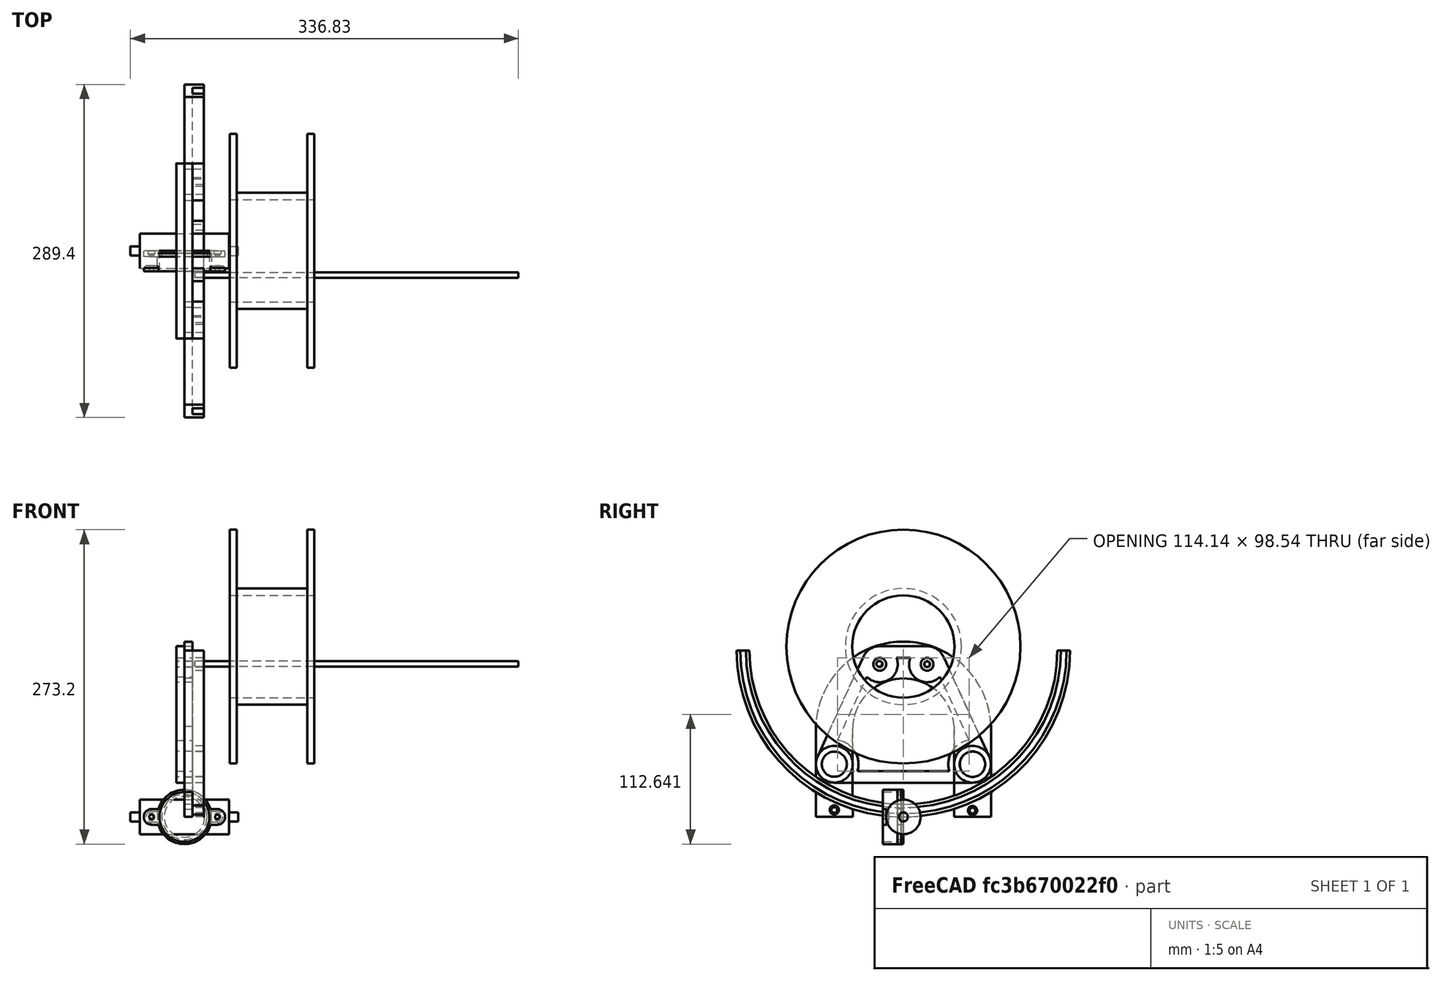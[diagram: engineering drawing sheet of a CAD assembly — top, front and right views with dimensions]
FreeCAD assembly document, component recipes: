
FREECAD ASSEMBLY — COMPONENT RECIPES ("filament dryer new version")

This assembly document has 17 components, labeled P0..P16 below (a component is one placed body or linked part). 17 of them carry a construction recipe — the FreeCAD feature program that regenerates the part from scratch, quoted from this document or its linked companion documents; the rest are supplied as boundary geometry only. No exploded tour is included for this assembly.
COMPONENT P0 — recipe-attached ("side bearing cilinders001", modeled in this document).
Construction recipe (the document's own serialized feature program — sketch geometry with constraints, then the solid features built on it; lengths are millimeters unless a unit is written):

FEATURE [Sketcher::SketchObject] Sketch004
  ArcFitTolerance = 1e-06
  AttachmentSupport = -> [XZ_Plane003]
  FullyConstrained = true
  MakeInternals = false
  MapMode = 5
  Placement = pos=(0,0,0) rot=(1,0,0;1.5708rad)
  expr: Constraints[17] = 3.925 mm
  sketch-geometry (8):
    g0: LineSegment StartX=-46.8333 StartY=0 StartZ=0 EndX=-46.8333 EndY=3.925 EndZ=0
    g1: LineSegment StartX=-46.8333 StartY=3.925 StartZ=0 EndX=-38.8333 EndY=3.925 EndZ=0
    g2: LineSegment StartX=-38.8333 StartY=3.925 StartZ=0 EndX=-38.8333 EndY=15 EndZ=0
    g3: LineSegment StartX=-38.8333 StartY=15 StartZ=0 EndX=38.8333 EndY=15 EndZ=0
    g4: LineSegment StartX=38.8333 StartY=15 StartZ=0 EndX=38.8333 EndY=3.925 EndZ=0
    g5: LineSegment StartX=38.8333 StartY=3.925 StartZ=0 EndX=46.8333 EndY=3.925 EndZ=0
    g6: LineSegment StartX=46.8333 StartY=3.925 StartZ=0 EndX=46.8333 EndY=1.2372e-12 EndZ=0
    g7: LineSegment StartX=-46.8333 StartY=0 StartZ=0 EndX=46.8333 EndY=1.2372e-12 EndZ=0
  constraints (23):
    c: PointOnObject(g0,g-1)
    c: Vertical(g0)
    c: Coincident(g1,g0)
    c: Horizontal(g1)
    c: Coincident(g2,g1)
    c: Vertical(g2)
    c: Coincident(g3,g2)
    c: Coincident(g4,g3)
    c: Coincident(g5,g4)
    c: Horizontal(g5)
    c: Vertical(g6)
    c: Vertical(g4)
    c: Equal(g2,g4)
    c: Equal(g0,g6)
    c: Symmetric(g2,g3,g-2)
    c: Coincident(g6,g5)
    c: DistanceX(g1,g1) = 8
    c: DistanceY(g0,g0) = 3.925
    c: Distance(g2,g-1) = 15
    c: Coincident(g7,g0)
    c: Coincident(g7,g6)
    c: DistanceX(g7,g7) = 93.6666
    c: Equal(g1,g5)
FEATURE [PartDesign::Revolution] Revolution001
  Angle = 360
  Angle2 = 60
  Axis = (1,0,0)
  Base = (0,0,0)
  Placement = pos=(0,0,0) rot=(1,0,0;1.5708rad)
  Profile = -> Sketch004
  ReferenceAxis = -> X_Axis003
  Refine = true
  Suppressed = false
  Type = 0
FEATURE [PartDesign::Body] Body003  label="side bearing cilinders"
  AllowCompound = false
  Group = -> [Sketch004,Revolution001]
  Origin = -> Origin003
  Tip = -> Revolution001
COMPONENT P1 — same part as P0; its construction recipe is shown at P0.
COMPONENT P2 — same part as P0; its construction recipe is shown at P0.
COMPONENT P3 — same part as P0; its construction recipe is shown at P0.
COMPONENT P4 — same part as P0; its construction recipe is shown at P0.
COMPONENT P5 — same part as P0; its construction recipe is shown at P0.
COMPONENT P6 — recipe-attached ("spool filament001", modeled in this document).
Construction recipe (the document's own serialized feature program — sketch geometry with constraints, then the solid features built on it; lengths are millimeters unless a unit is written):

FEATURE [Sketcher::SketchObject] Sketch
  ArcFitTolerance = 1e-06
  AttachmentSupport = -> [XZ_Plane]
  FullyConstrained = false
  MakeInternals = false
  MapMode = 5
  Placement = pos=(0,0,0) rot=(1,0,0;1.5708rad)
  sketch-geometry (8):
    g0: LineSegment StartX=-36.586 StartY=44.45 StartZ=0 EndX=36.586 EndY=44.45 EndZ=0
    g1: LineSegment StartX=-36.586 StartY=44.45 StartZ=0 EndX=-36.586 EndY=101.6 EndZ=0
    g2: LineSegment StartX=36.586 StartY=44.45 StartZ=0 EndX=36.586 EndY=101.6 EndZ=0
    g3: LineSegment StartX=-36.586 StartY=101.6 StartZ=0 EndX=-30.586 EndY=101.6 EndZ=0
    g4: LineSegment StartX=-30.586 StartY=101.6 StartZ=0 EndX=-30.586 EndY=50.45 EndZ=0
    g5: LineSegment StartX=30.586 StartY=101.6 StartZ=0 EndX=30.586 EndY=50.45 EndZ=0
    g6: LineSegment StartX=30.586 StartY=101.6 StartZ=0 EndX=36.586 EndY=101.6 EndZ=0
    g7: LineSegment StartX=-30.586 StartY=50.45 StartZ=0 EndX=30.586 EndY=50.45 EndZ=0
  constraints (21):
    c: Distance(g0) = 73.172
    c: Distance(g-1,g0) = 44.45
    c: Symmetric(g0,g0,g-2)
    c: Coincident(g1,g0)
    c: Vertical(g1)
    c: Coincident(g2,g0)
    c: Vertical(g2)
    c: Distance(g1,g-1) = 101.6
    c: Coincident(g3,g1)
    c: Coincident(g6,g2)
    c: Horizontal(g3)
    c: Vertical(g4)
    c: Vertical(g5)
    c: Symmetric(g5,g4,g-2)
    c: Distance(g1,g4) = 6
    c: Coincident(g3,g4)
    c: PointOnObject(g6,g5)
    c: Horizontal(g7)
    c: Distance(g0,g7) = 6
    c: Coincident(g4,g7)
    c: Coincident(g5,g7)
FEATURE [PartDesign::Revolution] Revolution
  Angle = 360
  Angle2 = 60
  Axis = (1,0,0)
  Base = (0,0,0)
  Placement = pos=(0,0,0) rot=(1,0,0;1.5708rad)
  Profile = -> Sketch
  ReferenceAxis = -> X_Axis
  Refine = true
  Reversed = true
  Suppressed = false
  Type = 0
FEATURE [PartDesign::Body] Body  label="spool filament"
  AllowCompound = false
  Group = -> [Sketch,Revolution]
  Origin = -> Origin
  Placement = pos=(76,0,148) rot=(0,0,1;0rad)
  Tip = -> Revolution
COMPONENT P7 — same part as P6; its construction recipe is shown at P6.
COMPONENT P8 — same part as P6; its construction recipe is shown at P6.
COMPONENT P9 — recipe-attached ("spool holder001", modeled in this document).
Construction recipe (the document's own serialized feature program — sketch geometry with constraints, then the solid features built on it; lengths are millimeters unless a unit is written):

FEATURE [Sketcher::SketchObject] Sketch001
  ArcFitTolerance = 1e-06
  AttachmentSupport = -> [YZ_Plane001]
  FullyConstrained = false
  MakeInternals = false
  MapMode = 5
  Placement = pos=(0,0,0) rot=(0.57735,0.57735,0.57735;2.0944rad)
  expr: Constraints[3] = 133.7 * 2 mm
  sketch-geometry (31):
    g0: Circle CenterX=-60 CenterY=45.7733 CenterZ=0 NormalX=0 NormalY=0 NormalZ=1 AngleXU=0 Radius=11.075
    g1: Circle CenterX=60 CenterY=45.7733 CenterZ=0 NormalX=0 NormalY=0 NormalZ=1 AngleXU=0 Radius=11.075
    g2: ArcOfCircle CenterX=0 CenterY=144.7 CenterZ=0 NormalX=0 NormalY=0 NormalZ=1 AngleXU=0 Radius=133.7 StartAngle=3.14159 EndAngle=4.10707
    g3: LineSegment [constr] StartX=-133.7 StartY=144.7 StartZ=0 EndX=133.7 EndY=144.7 EndZ=0
    g4: LineSegment [constr] StartX=-133.7 StartY=144.7 StartZ=0 EndX=133.7 EndY=144.7 EndZ=0
    g5: ArcOfCircle CenterX=0 CenterY=144.7 CenterZ=0 NormalX=0 NormalY=0 NormalZ=1 AngleXU=0 Radius=144.7 StartAngle=3.14159 EndAngle=4.15941
    g6: LineSegment StartX=-133.7 StartY=144.7 StartZ=0 EndX=-144.7 EndY=144.7 EndZ=0
    g7: LineSegment StartX=133.7 StartY=144.7 StartZ=0 EndX=144.7 EndY=144.7 EndZ=0
    g8: LineSegment StartX=-76.0782 StartY=46.2231 StartZ=0 EndX=-76.0782 EndY=34.7555 EndZ=0
    g9: LineSegment StartX=76.0296 StartY=48.9403 StartZ=0 EndX=76.0296 EndY=34.7219 EndZ=0
    g10: LineSegment StartX=-76 StartY=21.5656 StartZ=0 EndX=-76 EndY=0 EndZ=0
    g11: LineSegment StartX=76 StartY=21.5656 StartZ=0 EndX=76 EndY=0 EndZ=0
    g12: LineSegment StartX=-44.0838 StartY=46.2231 StartZ=0 EndX=-44.0838 EndY=18.4768 EndZ=0
    g13: LineSegment StartX=44 StartY=48.9403 StartZ=0 EndX=44 EndY=18.4475 EndZ=0
    g14: LineSegment StartX=-44 StartY=6.85193 StartZ=0 EndX=-44 EndY=0 EndZ=0
    g15: LineSegment StartX=43.9992 StartY=6.85167 StartZ=0 EndX=43.9992 EndY=0 EndZ=0
    g16: LineSegment StartX=-76 StartY=0 StartZ=0 EndX=-44 EndY=0 EndZ=0
    g17: LineSegment StartX=43.9992 StartY=0 StartZ=0 EndX=76 EndY=0 EndZ=0
    g18: ArcOfCircle CenterX=0 CenterY=144.7 CenterZ=0 NormalX=0 NormalY=0 NormalZ=1 AngleXU=0 Radius=144.7 StartAngle=4.40342 EndAngle=5.02135
    g19: ArcOfCircle CenterX=0 CenterY=144.7 CenterZ=0 NormalX=0 NormalY=0 NormalZ=1 AngleXU=0 Radius=144.7 StartAngle=5.26537 EndAngle=6.28319
    g20: ArcOfCircle CenterX=0 CenterY=144.7 CenterZ=0 NormalX=0 NormalY=0 NormalZ=1 AngleXU=0 Radius=133.7 StartAngle=5.31726 EndAngle=6.28319
    g21: ArcOfCircle CenterX=0 CenterY=144.7 CenterZ=0 NormalX=0 NormalY=0 NormalZ=1 AngleXU=0 Radius=133.7 StartAngle=4.37638 EndAngle=5.04773
    g22: LineSegment [constr] StartX=-76.0782 StartY=46.2231 StartZ=0 EndX=-44.0838 EndY=46.2231 EndZ=0
    g23: LineSegment [constr] StartX=44 StartY=48.9403 StartZ=0 EndX=76.0296 EndY=48.9403 EndZ=0
    g24: LineSegment StartX=-76.0782 StartY=46.2231 StartZ=0 EndX=-76.0782 EndY=76.2231 EndZ=0
    g25: LineSegment StartX=76.0296 StartY=48.9403 StartZ=0 EndX=76.0296 EndY=78.9403 EndZ=0
    g26: LineSegment StartX=44 StartY=48.9403 StartZ=0 EndX=44 EndY=78.9403 EndZ=0
    g27: LineSegment StartX=-44.0838 StartY=46.2231 StartZ=0 EndX=-44.0838 EndY=76.2231 EndZ=0
    g28: LineSegment [constr] StartX=-44.0838 StartY=76.2231 StartZ=0 EndX=0 EndY=76.2231 EndZ=0
    g29: ArcOfCircle CenterX=0 CenterY=76.2231 CenterZ=0 NormalX=0 NormalY=0 NormalZ=1 AngleXU=0 Radius=44.0838 StartAngle=0.061677 EndAngle=3.14159
    g30: ArcOfCircle CenterX=0 CenterY=76.2231 CenterZ=0 NormalX=0 NormalY=0 NormalZ=1 AngleXU=0 Radius=76.0782 StartAngle=0.0357239 EndAngle=3.14159
  constraints (80):
    c: Diameter(g0) = 22.15
    c: Equal(g1,g0)
    c: Symmetric(g0,g1,g-2)
    c: Diameter(g2) = 267.4
    c: PointOnObject(g2,g-2)
    c: Horizontal(g3)
    c: PointOnObject(g2,g3)
    c: Coincident(g4,g3)
    c: Coincident(g4,g3)
    c: Coincident(g20,g3)
    c: Coincident(g2,g3)
    c: Distance(g2,g-1) = 11
    c: Coincident(g5,g2)
    c: PointOnObject(g-1,g18)
    c: Coincident(g6,g2)
    c: Horizontal(g6)
    c: Coincident(g7,g20)
    c: Horizontal(g7)
    c: Coincident(g19,g7)
    c: Coincident(g5,g6)
    c: PointOnObject(g10,g-1)
    c: Vertical(g8)
    c: PointOnObject(g11,g-1)
    c: Vertical(g9)
    c: Distance(g0,g-2) = 60
    c: PointOnObject(g9,g20)
    c: PointOnObject(g11,g19)
    c: PointOnObject(g14,g-1)
    c: Vertical(g12)
    c: PointOnObject(g15,g-1)
    c: Vertical(g13)
    c: PointOnObject(g12,g21)
    c: PointOnObject(g14,g18)
    c: Coincident(g16,g10)
    c: Coincident(g16,g14)
    c: Coincident(g17,g15)
    c: Coincident(g17,g11)
    c: Equal(g5,g18)
    c: Coincident(g5,g10)
    c: PointOnObject(g18,g14)
    c: Coincident(g5,g18)
    c: Equal(g18,g19)
    c: Coincident(g18,g15)
    c: PointOnObject(g19,g11)
    c: Coincident(g18,g19)
    c: Equal(g2,g20)
    c: Coincident(g21,g13)
    c: PointOnObject(g20,g9)
    c: Coincident(g2,g20)
    c: Equal(g2,g21)
    c: Coincident(g2,g8)
    c: PointOnObject(g21,g12)
    c: Coincident(g2,g21)
    c: Coincident(g22,g8)
    c: Coincident(g22,g12)
    c: Horizontal(g22)
    c: Coincident(g23,g13)
    c: Coincident(g23,g9)
    c: Horizontal(g23)
    c: Distance(g24) = 30
    c: Coincident(g24,g8)
    c: Vertical(g24)
    c: Coincident(g25,g9)
    c: Vertical(g25)
    c: Coincident(g26,g13)
    c: Vertical(g26)
    c: Coincident(g27,g12)
    c: Vertical(g27)
    c: Equal(g24,g27)
    c: Equal(g27,g26)
    c: Equal(g26,g25)
    c: Coincident(g28,g27)
    c: PointOnObject(g28,g-2)
    c: Horizontal(g28)
    c: Coincident(g29,g28)
    c: Coincident(g29,g27)
    c: Coincident(g29,g26)
    c: Coincident(g30,g28)
    c: Coincident(g30,g24)
    c: Coincident(g30,g25)
FEATURE [PartDesign::Pad] Pad
  Direction = (1,0,0)
  Length = 7
  Length2 = 10
  Placement = pos=(0,0,0) rot=(1,1,1;2.0944rad)
  Profile = -> Sketch001
  ReferenceAxis = -> Sketch001 [N_Axis]
  Refine = true
  Suppressed = false
  Type = 0
FEATURE [Sketcher::SketchObject] Sketch002
  ArcFitTolerance = 1e-06
  AttachmentSupport = -> [Pad]
  ExternalGeometry = -> [Pad]
  FullyConstrained = false
  MakeInternals = false
  MapMode = 5
  Placement = pos=(7,0,0) rot=(0.57735,0.57735,0.57735;2.0944rad)
  sketch-geometry (24):
    g0: ArcOfCircle CenterX=2.39e-14 CenterY=144.7 CenterZ=0 NormalX=0 NormalY=0 NormalZ=1 AngleXU=0 Radius=133.7 StartAngle=3.14159 EndAngle=6.28319
    g1: ArcOfCircle CenterX=2.39e-14 CenterY=144.7 CenterZ=0 NormalX=0 NormalY=0 NormalZ=1 AngleXU=0 Radius=144.7 StartAngle=3.14159 EndAngle=6.28319
    g2: ArcOfCircle CenterX=2.39e-14 CenterY=144.7 CenterZ=0 NormalX=0 NormalY=0 NormalZ=1 AngleXU=0 Radius=141.7 StartAngle=3.14159 EndAngle=6.28319
    g3: ArcOfCircle CenterX=2.39e-14 CenterY=144.7 CenterZ=0 NormalX=0 NormalY=0 NormalZ=1 AngleXU=0 Radius=136.7 StartAngle=3.14159 EndAngle=6.28319
    g4: LineSegment StartX=133.7 StartY=144.7 StartZ=0 EndX=136.7 EndY=144.7 EndZ=0
    g5: LineSegment StartX=141.7 StartY=144.7 StartZ=0 EndX=144.7 EndY=144.7 EndZ=0
    g6: LineSegment StartX=-136.7 StartY=144.7 StartZ=0 EndX=-133.7 EndY=144.7 EndZ=0
    g7: LineSegment StartX=-144.7 StartY=144.7 StartZ=0 EndX=-141.7 EndY=144.7 EndZ=0
    g8: Circle CenterX=-60 CenterY=6 CenterZ=0 NormalX=0 NormalY=0 NormalZ=1 AngleXU=0 Radius=2.5
    g9: Circle CenterX=-60 CenterY=6 CenterZ=0 NormalX=0 NormalY=0 NormalZ=1 AngleXU=0 Radius=4
    g10: LineSegment [constr] StartX=-60 StartY=10.7501 StartZ=0 EndX=-60 EndY=-7.18174 EndZ=0
    g11: Circle CenterX=60 CenterY=5.5 CenterZ=0 NormalX=0 NormalY=0 NormalZ=1 AngleXU=0 Radius=2.5
    g12: Circle CenterX=60 CenterY=5.5 CenterZ=0 NormalX=0 NormalY=0 NormalZ=1 AngleXU=0 Radius=4
    g13: Circle CenterX=-60 CenterY=45.7733 CenterZ=0 NormalX=0 NormalY=0 NormalZ=1 AngleXU=0 Radius=10.901
    g14: Circle CenterX=-60 CenterY=45.7733 CenterZ=0 NormalX=0 NormalY=0 NormalZ=1 AngleXU=0 Radius=16
    g15: Circle CenterX=59.9992 CenterY=45.7733 CenterZ=0 NormalX=0 NormalY=0 NormalZ=1 AngleXU=0 Radius=16
    g16: Circle CenterX=59.9992 CenterY=45.7733 CenterZ=0 NormalX=0 NormalY=0 NormalZ=1 AngleXU=0 Radius=11.0656
    g17: LineSegment [constr] StartX=0 StartY=152.301 StartZ=0 EndX=0 EndY=120.307 EndZ=0
    g18: LineSegment [constr] StartX=0 StartY=136.304 StartZ=0 EndX=37.5871 EndY=136.304 EndZ=0
    g19: Circle CenterX=-20.575 CenterY=132.671 CenterZ=0 NormalX=0 NormalY=0 NormalZ=1 AngleXU=0 Radius=2.575
    g20: Circle CenterX=-20.575 CenterY=132.671 CenterZ=0 NormalX=0 NormalY=0 NormalZ=1 AngleXU=0 Radius=5.575
    g21: ArcOfCircle [constr] CenterX=8.5e-15 CenterY=76.2231 CenterZ=0 NormalX=0 NormalY=0 NormalZ=1 AngleXU=0 Radius=60.081 StartAngle=0.738747 EndAngle=2.47765
    g22: Circle CenterX=20.575 CenterY=132.671 CenterZ=0 NormalX=0 NormalY=0 NormalZ=1 AngleXU=0 Radius=5.575
    g23: Circle CenterX=20.575 CenterY=132.671 CenterZ=0 NormalX=0 NormalY=0 NormalZ=1 AngleXU=0 Radius=2.575
  constraints (50):
    c: Coincident(g0,g-5)
    c: Coincident(g0,g-3)
    c: Coincident(g0,g-4)
    c: Coincident(g1,g0)
    c: Coincident(g1,g-3)
    c: Coincident(g1,g-4)
    c: Coincident(g2,g0)
    c: PointOnObject(g2,g-3)
    c: PointOnObject(g2,g-4)
    c: Coincident(g3,g0)
    c: PointOnObject(g3,g-3)
    c: PointOnObject(g3,g-4)
    c: Distance(g2,g1) = 3
    c: Distance(g3,g0) = 3
    c: Coincident(g4,g0)
    c: Coincident(g4,g3)
    c: Coincident(g5,g2)
    c: Coincident(g5,g1)
    c: Coincident(g6,g3)
    c: Coincident(g6,g0)
    c: Coincident(g7,g1)
    c: Coincident(g7,g2)
    c: Coincident(g9,g8)
    c: Diameter(g8) = 5
    c: Distance(g9,g-1) = 2
    c: Symmetric(g-7,g-6,g10)
    c: PointOnObject(g8,g10)
    c: Coincident(g12,g11)
    c: Diameter(g11) = 5
    c: Diameter(g12) = 8
    c: Tangent(g13,g-8) = -1.5708
    c: Coincident(g14,g13)
    c: Coincident(g16,g15)
    c: PointOnObject(g17,g-2)
    c: PointOnObject(g17,g-2)
    c: PointOnObject(g17,g-10)
    c: PointOnObject(g17,g-11)
    c: Symmetric(g17,g17,g18)
    c: PointOnObject(g18,g17)
    c: Diameter(g19) = 5.15
    c: Coincident(g20,g19)
    c: Distance(g20,g19) = 3
    c: Coincident(g21,g-11)
    c: PointOnObject(g18,g21)
    c: PointOnObject(g19,g21)
    c: Distance(g20,g17) = 15
    c: Diameter(g23) = 5.15
    c: Coincident(g22,g23)
    c: Distance(g22,g23) = 3
    c: Equal(g9,g12)
FEATURE [PartDesign::Pad] Pad001
  BaseFeature = -> Pad
  Direction = (1,0,0)
  Length = 10
  Length2 = 10
  Placement = pos=(0,0,0) rot=(1,1,1;2.0944rad)
  Profile = -> Sketch002
  ReferenceAxis = -> Sketch002 [N_Axis]
  Refine = true
  Suppressed = false
  Type = 0
FEATURE [PartDesign::Body] Body001  label="spool holder"
  AllowCompound = false
  Group = -> [Sketch001,Pad,Sketch002,Pad001]
  Origin = -> Origin001
  Tip = -> Pad001
COMPONENT P10 — same part as P9; its construction recipe is shown at P9.
COMPONENT P11 — recipe-attached ("spoon holder joins001", modeled in this document).
Construction recipe (the document's own serialized feature program — sketch geometry with constraints, then the solid features built on it; lengths are millimeters unless a unit is written):

FEATURE [Sketcher::SketchObject] Sketch003
  ArcFitTolerance = 1e-06
  AttachmentSupport = -> [YZ_Plane002]
  FullyConstrained = false
  MakeInternals = false
  MapMode = 5
  Placement = pos=(0,0,0) rot=(0.57735,0.57735,0.57735;2.0944rad)
  sketch-geometry (2):
    g0: Circle [constr] CenterX=0 CenterY=0 CenterZ=0 NormalX=0 NormalY=0 NormalZ=1 AngleXU=0 Radius=0
    g1: Circle CenterX=0 CenterY=0 CenterZ=0 NormalX=0 NormalY=0 NormalZ=1 AngleXU=0 Radius=2.5
  constraints (2):
    c: Coincident(g1,g0)
    c: Diameter(g1) = 5
FEATURE [PartDesign::Pad] Pad002
  Direction = (1,0,0)
  Length = 281
  Length2 = 10
  Placement = pos=(0,0,0) rot=(1,1,1;2.0944rad)
  Profile = -> Sketch003
  ReferenceAxis = -> Sketch003 [N_Axis]
  Refine = true
  Suppressed = false
  Type = 0
FEATURE [PartDesign::Body] Body002  label="spoon holder joins"
  AllowCompound = false
  Group = -> [Sketch003,Pad002]
  Origin = -> Origin002
  Placement = pos=(9,-21,133) rot=(0,0,1;0rad)
  Tip = -> Pad002
COMPONENT P12 — same part as P11; its construction recipe is shown at P11.
COMPONENT P13 — same part as P11; its construction recipe is shown at P11.
COMPONENT P14 — same part as P11; its construction recipe is shown at P11.
COMPONENT P15 — recipe-attached ("spoon holder middle section001", modeled in this document).
Construction recipe (the document's own serialized feature program — sketch geometry with constraints, then the solid features built on it; lengths are millimeters unless a unit is written):

FEATURE [PartDesign::SubShapeBinder] Binder
  BindCopyOnChange = 0
  BindMode = 0
  ClaimChildren = false
  Context = -> Body004 [Binder.]
  Fuse = false
  MakeFace = true
  OffsetFill = false
  OffsetIntersection = false
  OffsetJoinType = 0
  OffsetOpenResult = false
  PartialLoad = false
  Refine = true
  Relative = true
  Support = -> [Body001[Pad001.Face33,Pad001.Face34]]
  _Version = 2
FEATURE [Sketcher::SketchObject] Sketch005
  ArcFitTolerance = 1e-06
  AttachmentSupport = -> [YZ_Plane004]
  ExternalGeometry = -> [Binder]
  FullyConstrained = false
  MakeInternals = false
  MapMode = 5
  Placement = pos=(0,0,0) rot=(0.57735,0.57735,0.57735;2.0944rad)
  sketch-geometry (24):
    g0: Circle CenterX=-60 CenterY=45.77 CenterZ=0 NormalX=0 NormalY=0 NormalZ=1 AngleXU=0 Radius=11
    g1: Circle CenterX=59.9999 CenterY=45.77 CenterZ=0 NormalX=0 NormalY=0 NormalZ=1 AngleXU=0 Radius=11
    g2: LineSegment [constr] StartX=-60 StartY=45.77 StartZ=0 EndX=-60 EndY=0 EndZ=0
    g3: ArcOfCircle CenterX=-60 CenterY=45.77 CenterZ=0 NormalX=0 NormalY=0 NormalZ=1 AngleXU=0 Radius=16 StartAngle=2.71191 EndAngle=4.71239
    g4: ArcOfCircle CenterX=59.9999 CenterY=45.77 CenterZ=0 NormalX=0 NormalY=0 NormalZ=1 AngleXU=0 Radius=16 StartAngle=4.71239 EndAngle=6.71287
    g5: LineSegment StartX=-39.8754 StartY=39.77 StartZ=0 EndX=39.8753 EndY=39.77 EndZ=0
    g6: ArcOfCircle CenterX=59.9999 CenterY=45.77 CenterZ=0 NormalX=0 NormalY=0 NormalZ=1 AngleXU=0 Radius=21 StartAngle=1.71073 EndAngle=3.43134
    g7: ArcOfCircle CenterX=-60 CenterY=45.77 CenterZ=0 NormalX=0 NormalY=0 NormalZ=1 AngleXU=0 Radius=21 StartAngle=5.99343 EndAngle=7.71405
    g8: GeomPoint [constr] X=0 Y=151.304 Z=0
    g9: Circle CenterX=-20.575 CenterY=132.671 CenterZ=0 NormalX=0 NormalY=0 NormalZ=1 AngleXU=0 Radius=2.575
    g10: Circle CenterX=20.575 CenterY=132.671 CenterZ=0 NormalX=0 NormalY=0 NormalZ=1 AngleXU=0 Radius=2.36628
    g11: Circle [constr] CenterX=-20.575 CenterY=132.671 CenterZ=0 NormalX=0 NormalY=0 NormalZ=1 AngleXU=0 Radius=5.63976
    g12: Circle [constr] CenterX=20.575 CenterY=132.671 CenterZ=0 NormalX=0 NormalY=0 NormalZ=1 AngleXU=0 Radius=5.575
    g13: LineSegment StartX=-74.5456 StartY=52.4353 StartZ=0 EndX=-34.7931 EndY=139.186 EndZ=0
    g14: LineSegment StartX=74.5455 StartY=52.4353 StartZ=0 EndX=34.7931 EndY=139.186 EndZ=0
    g15: ArcOfCircle CenterX=-20.575 CenterY=132.671 CenterZ=0 NormalX=0 NormalY=0 NormalZ=1 AngleXU=0 Radius=15.6398 StartAngle=3.91379 EndAngle=6.6521
    g16: ArcOfCircle CenterX=20.575 CenterY=132.671 CenterZ=0 NormalX=0 NormalY=0 NormalZ=1 AngleXU=0 Radius=15.6398 StartAngle=0.429681 EndAngle=1.5708
    g17: LineSegment StartX=-57.071 StartY=66.5647 StartZ=0 EndX=-31.779 EndY=121.759 EndZ=0
    g18: LineSegment StartX=57.071 StartY=66.5647 StartZ=0 EndX=31.779 EndY=121.759 EndZ=0
    g19: LineSegment StartX=-5.9875 StartY=138.311 StartZ=0 EndX=5.9875 EndY=138.311 EndZ=0
    g20: ArcOfCircle CenterX=-20.575 CenterY=132.671 CenterZ=0 NormalX=0 NormalY=0 NormalZ=1 AngleXU=0 Radius=15.6398 StartAngle=1.5708 EndAngle=2.71191
    g21: ArcOfCircle CenterX=20.575 CenterY=132.671 CenterZ=0 NormalX=0 NormalY=0 NormalZ=1 AngleXU=0 Radius=15.6398 StartAngle=2.77268 EndAngle=5.51099
    g22: LineSegment StartX=-20.575 StartY=148.311 StartZ=0 EndX=20.575 EndY=148.311 EndZ=0
    g23: LineSegment StartX=-60 StartY=29.77 StartZ=0 EndX=59.9999 EndY=29.77 EndZ=0
  constraints (52):
    c: Diameter(g0) = 22
    c: PointOnObject(g2,g-1)
    c: Block(g1)
    c: PointOnObject(g3,g2)
    c: Distance(g0,g3) = 5
    c: Distance(g1,g4) = 5
    c: Block(g2)
    c: Coincident(g0,g2)
    c: Coincident(g3,g0)
    c: Coincident(g4,g1)
    c: Horizontal(g5)
    c: Coincident(g6,g1)
    c: Coincident(g6,g5)
    c: Coincident(g7,g0)
    c: Coincident(g7,g5)
    c: Distance(g0,g7) = 10
    c: Distance(g6,g1) = 10
    c: PointOnObject(g8,g-2)
    c: Coincident(g9,g-5)
    c: Equal(g9,g-5)
    c: Coincident(g10,g-4)
    c: Coincident(g11,g9)
    c: Coincident(g12,g10)
    c: Tangent(g12,g-4)
    c: Coincident(g15,g9)
    c: Coincident(g16,g10)
    c: Distance(g11,g15) = 10
    c: Block(g11)
    c: Tangent(g4,g14) = -1.5708
    c: Tangent(g3,g13) = 1.5708
    c: Coincident(g17,g7)
    c: Coincident(g18,g6)
    c: Parallel(g18,g14)
    c: Parallel(g17,g13)
    c: Distance(g13,g17) = 10
    c: Distance(g14,g18) = 10
    c: Coincident(g20,g13) = 1.5708
    c: Coincident(g15,g17)
    c: Coincident(g21,g18)
    c: Tangent(g16,g14) = -1.5708
    c: PointOnObject(g19,g21)
    c: Coincident(g15,g19)
    c: Coincident(g15,g20)
    c: Equal(g16,g21)
    c: PointOnObject(g21,g19)
    c: Coincident(g16,g21)
    c: Coincident(g22,g20)
    c: Coincident(g22,g16)
    c: Horizontal(g22)
    c: Coincident(g23,g3)
    c: Tangent(g23,g4) = -1.5708
    c: Horizontal(g23)
FEATURE [PartDesign::Pad] Pad008
  Direction = (1,0,0)
  Length = 14
  Length2 = 10
  Midplane = true
  Placement = pos=(0,0,0) rot=(1,1,1;2.0944rad)
  Profile = -> Sketch005
  ReferenceAxis = -> Sketch005 [N_Axis]
  Refine = true
  Suppressed = false
  Type = 0
FEATURE [PartDesign::Body] Body004  label="spoon holder middle section"
  AllowCompound = false
  Group = -> [Sketch005,Binder,Pad008]
  Origin = -> Origin004
  Tip = -> Pad008
COMPONENT P16 — same part as P15; its construction recipe is shown at P15.
PROVENANCE & LICENSES
A FreeCAD (.FCStd) document from a public repository crawl; recipes are the document's own serialized feature recipes (and, for linked parts, companion documents' recipes).
License: as declared in the source repository (recorded in the dataset sidecar).
